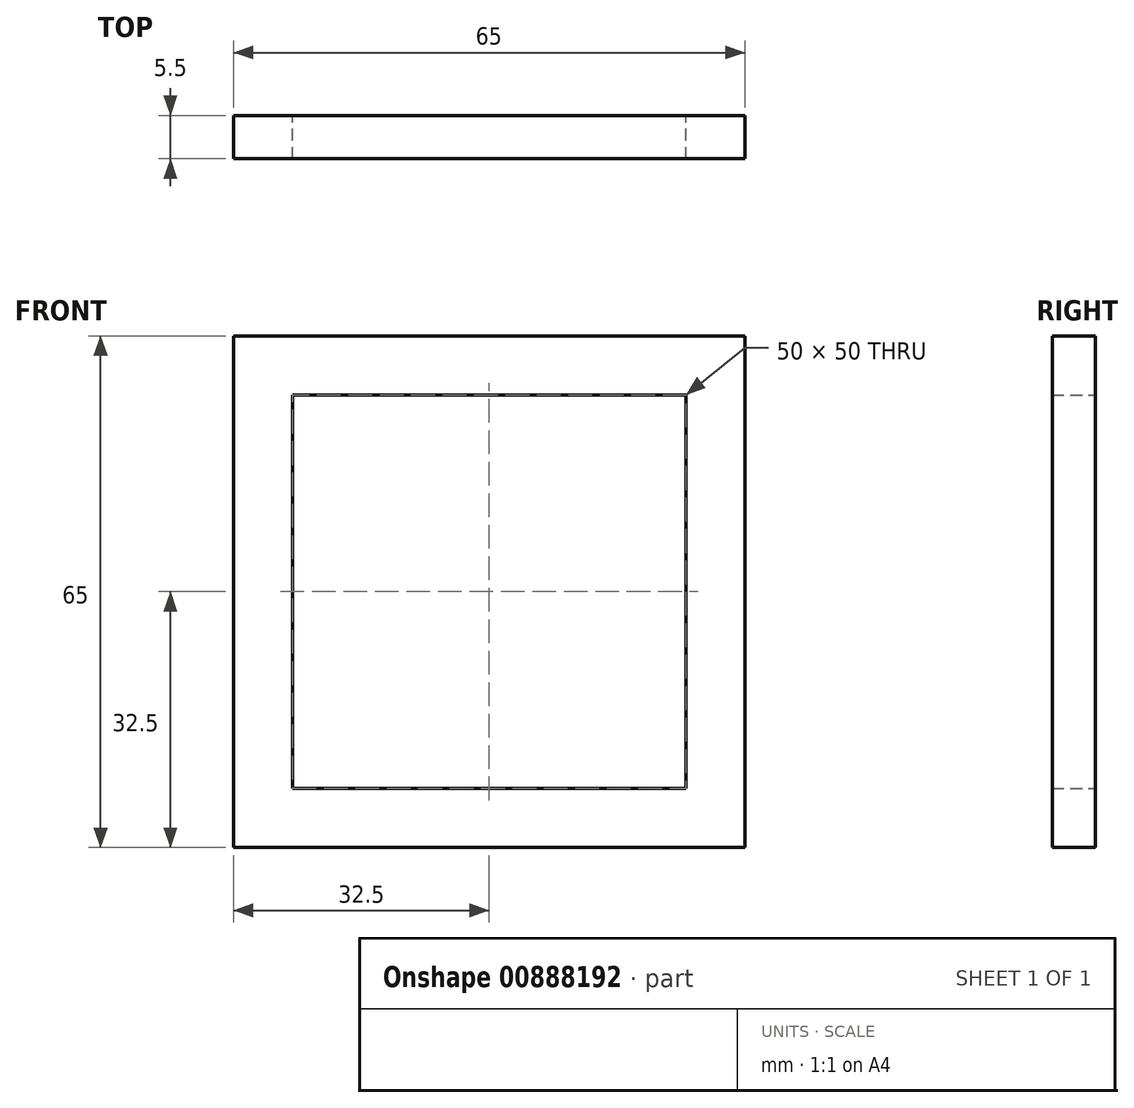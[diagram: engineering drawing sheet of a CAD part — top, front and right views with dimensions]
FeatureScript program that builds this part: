
annotation { "Feature Type Name" : "Feature", "Feature Type Description" : "" }
export const myFeature = defineFeature(function(context is Context, id is Id, definition is map)
    precondition{}
    {
        {
            var Q0;
            Q0=qCreatedBy(makeId("Front.planeOp"),FACE);
            var sketch = newSketch(context, id + "F0", { "sketchPlane" : qUnion([Q0])});
            skLineSegment(sketch, "E0.bottom", {"start": v(-32.5, 32.5) * mm, "end": v(32.5, 32.5) * mm});
            skLineSegment(sketch, "E0.top", {"start": v(-32.5, -32.5) * mm, "end": v(32.5, -32.5) * mm});
            skLineSegment(sketch, "E0.left", {"start": v(-32.5, 32.5) * mm, "end": v(-32.5, -32.5) * mm});
            skLineSegment(sketch, "E0.right", {"start": v(32.5, 32.5) * mm, "end": v(32.5, -32.5) * mm});
            skLineSegment(sketch, "E1.bottom", {"start": v(-25, 25) * mm, "end": v(25, 25) * mm});
            skLineSegment(sketch, "E1.top", {"start": v(-25, -25) * mm, "end": v(25, -25) * mm});
            skLineSegment(sketch, "E1.left", {"start": v(-25, 25) * mm, "end": v(-25, -25) * mm});
            skLineSegment(sketch, "E1.right", {"start": v(25, 25) * mm, "end": v(25, -25) * mm});
            skSolve(sketch);
        }
        {
            var Q0;
            Q0=makeQuery(id+"F0.imprint","IMPRINT",FACE,{"disambiguationData":[TD([[makeQuery(id+"F0.imprint","IMPRINT",EDGE,{"derivedFrom":sQuery(id+"F0.wireOp",EDGE,"E0.bottom")}),-1.0]])]});
            extrude(context, id + "F1", {"entities" : qUnion([Q0]), "endBound" : BoundingType.SYMMETRIC, "depth" : 5.5 * mm, "offsetDistance" : 25 * mm});
        }
    });
